# Revit family: SDP-883 Поворотное устройство
name_source: partatom
category: Оборудование
revit_build: Autodesk Revit 2017 (Build: 20170118_1100(x64)
units: mm (PartAtom-declared; Revit-internal decimal feet)

## family parameters
Всегда вертикально = Нет
На основе рабочей плоскости = Нет
Общий = Нет
При загрузке вырезать с полостями = Нет
Размер круглого соединителя = Использовать диаметр
Тип детали = Нормальный
Точка расчета площади = Нет

## types (1)
- SDP-883 Поворотное устройство
    ADSK_URL страницы изделия = https://stilsoft.ru
    ADSK_Единица измерения = шт.
    ADSK_Завод-изготовитель = ООО «Основа Безопасности»
    ADSK_Количество = 1
    ADSK_Марка = СТВФ.426459.074
    ADSK_Масса = 22
    ADSK_Наименование = Поворотное устройство SDP-883
    ADSK_Размер_Высота = 404 мм
    ADSK_Размер_Длина = 450 мм
    ADSK_Размер_Ширина = 233 мм
    d_короба = 20 мм
    Выходное напряжение постоянного тока, В = 24
    Защита от внешних воздействий = IP66
    Интерфейс управления = Ethernet 100 Мбит/с
    Количество предустановок, шт. = 30
    Максимальная нагрузка, кг = 50
    Напряжение электропитания постоянного тока, В = 24±10%
    Потребляемый ток в режиме экономии энергии, не более, А = 1 А
    Потребляемый ток, не более, А = 5 А
    Режим работы = непрерывный
    Скорость поворота по вертикали, град/сек. = 0,01-15
    Скорость поворота по горизонтали, град/сек. = 0,01-30
    Точность позиционирования, град. = 0.5
    Угол обзора по вертикали, град. = ±45
    Угол поворота по горизонтали, град. = 360.00°
